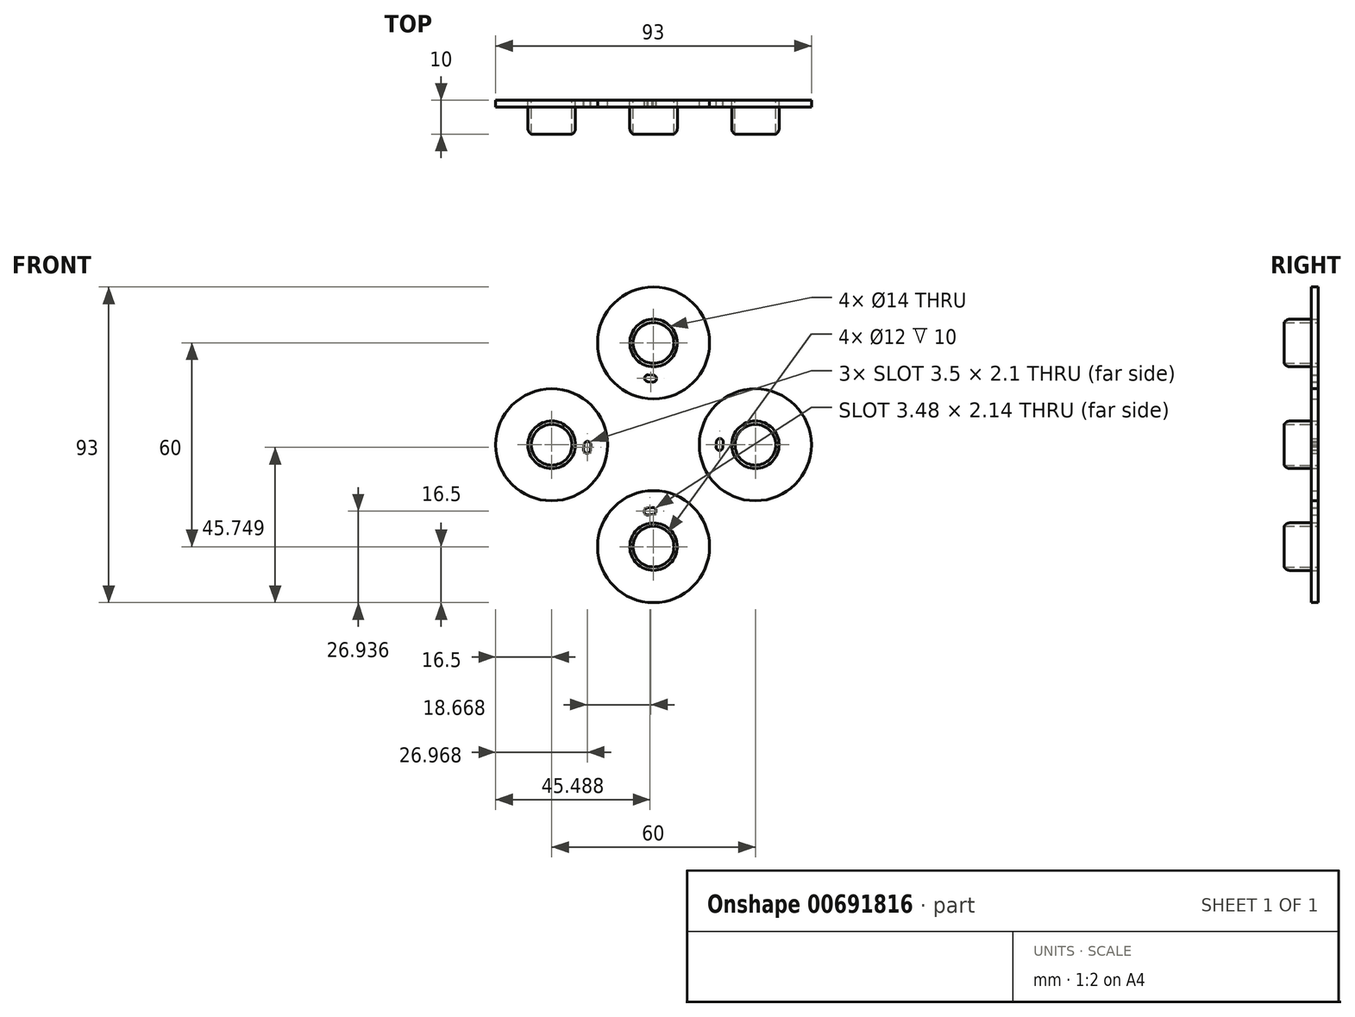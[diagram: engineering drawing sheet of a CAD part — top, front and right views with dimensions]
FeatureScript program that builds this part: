
annotation { "Feature Type Name" : "Feature", "Feature Type Description" : "" }
export const myFeature = defineFeature(function(context is Context, id is Id, definition is map)
    precondition{}
    {
        {
            var Q0;
            Q0=qCreatedBy(makeId("Front.planeOp"),FACE);
            var sketch = newSketch(context, id + "F0", { "sketchPlane" : qUnion([Q0])});
            skCircle(sketch, "E0", {"center": v(0, 0) * mm, "radius": 50 * mm});
            skCircle(sketch, "E1", {"center": v(0, 30) * mm, "radius": 16.5 * mm});
            skCircle(sketch, "E2", {"center": v(0, -30) * mm, "radius": 16.5 * mm});
            skCircle(sketch, "E3", {"center": v(-30, 0) * mm, "radius": 16.5 * mm});
            skCircle(sketch, "E4", {"center": v(30, 0) * mm, "radius": 16.5 * mm});
            skCircle(sketch, "E5", {"center": v(-30, 0) * mm, "radius": 12.5 * mm});
            skCircle(sketch, "E6", {"center": v(0, -30) * mm, "radius": 12.5 * mm});
            skCircle(sketch, "E7", {"center": v(30, 0) * mm, "radius": 12.5 * mm});
            skCircle(sketch, "E8", {"center": v(0, 30) * mm, "radius": 12.5 * mm});
            skCircle(sketch, "E9", {"center": v(-30, 0) * mm, "radius": 7 * mm});
            skCircle(sketch, "E10", {"center": v(0, 30) * mm, "radius": 7 * mm});
            skCircle(sketch, "E11", {"center": v(30, 0) * mm, "radius": 7 * mm});
            skCircle(sketch, "E12", {"center": v(0, -30) * mm, "radius": 7 * mm});
            skCircle(sketch, "E13", {"center": v(0, 30) * mm, "radius": 6 * mm});
            skCircle(sketch, "E14", {"center": v(-30, 0) * mm, "radius": 6 * mm});
            skCircle(sketch, "E15", {"center": v(0, -30) * mm, "radius": 6 * mm});
            skCircle(sketch, "E16", {"center": v(30, 0) * mm, "radius": 0.5 * mm});
            skCircle(sketch, "E17", {"center": v(-19.47, 0) * mm, "radius": 1 * mm});
            skCircle(sketch, "E18", {"center": v(-19.58, -1.5) * mm, "radius": 1 * mm});
            skLineSegment(sketch, "E19", {"start": v(-20.47, 0) * mm, "end": v(-20.58, -1.42) * mm});
            skLineSegment(sketch, "E20", {"start": v(-18.47, 0) * mm, "end": v(-18.6, -1.66) * mm});
            skCircle(sketch, "E21", {"center": v(-1.76, -19.65) * mm, "radius": 1 * mm});
            skCircle(sketch, "E22", {"center": v(-0.26, -19.48) * mm, "radius": 1 * mm});
            skLineSegment(sketch, "E23", {"start": v(-1.58, -20.63) * mm, "end": v(-0.15, -20.47) * mm});
            skLineSegment(sketch, "E24", {"start": v(-1.94, -18.67) * mm, "end": v(-0.3, -18.48) * mm});
            skLineSegment(sketch, "E25.0", {"start": v(-0.26, -19.48) * mm, "end": v(-0.28, -19.37) * mm, "construction": true});
            skCircle(sketch, "E26", {"center": v(19.54, 0.84) * mm, "radius": 1 * mm});
            skCircle(sketch, "E27", {"center": v(19.42, -0.66) * mm, "radius": 1 * mm});
            skLineSegment(sketch, "E28", {"start": v(18.54, 0.84) * mm, "end": v(18.43, -0.58) * mm});
            skLineSegment(sketch, "E29", {"start": v(20.54, 0.84) * mm, "end": v(20.41, -0.82) * mm});
            skCircle(sketch, "E30", {"center": v(-0.11, 19.5) * mm, "radius": 1 * mm});
            skCircle(sketch, "E31", {"center": v(-1.61, 19.61) * mm, "radius": 1 * mm});
            skLineSegment(sketch, "E32", {"start": v(-0.11, 20.5) * mm, "end": v(-1.54, 20.61) * mm});
            skLineSegment(sketch, "E33", {"start": v(-0.11, 18.5) * mm, "end": v(-1.78, 18.63) * mm});
            skCircle(sketch, "E34", {"center": v(30, 0) * mm, "radius": 6 * mm});
            skSolve(sketch);
        }
        {
            var Q0;
            Q0=makeQuery(id+"F0.imprint","IMPRINT",FACE,{"disambiguationData":[TD([[makeQuery(id+"F0.imprint","IMPRINT",EDGE,{"derivedFrom":sQuery(id+"F0.wireOp",EDGE,"E9")}),1.0]])]});
            var Q1;
            Q1=makeQuery(id+"F0.imprint","IMPRINT",FACE,{"disambiguationData":[TD([[makeQuery(id+"F0.imprint","IMPRINT",EDGE,{"derivedFrom":sQuery(id+"F0.wireOp",EDGE,"E10")}),1.0]])]});
            var Q2;
            Q2=makeQuery(id+"F0.imprint","IMPRINT",FACE,{"disambiguationData":[TD([[makeQuery(id+"F0.imprint","IMPRINT",EDGE,{"derivedFrom":sQuery(id+"F0.wireOp",EDGE,"E11")}),1.0]])]});
            var Q3;
            Q3=makeQuery(id+"F0.imprint","IMPRINT",FACE,{"disambiguationData":[TD([[makeQuery(id+"F0.imprint","IMPRINT",EDGE,{"derivedFrom":sQuery(id+"F0.wireOp",EDGE,"E12")}),1.0]])]});
            extrude(context, id + "F1", {"entities" : qUnion([Q0, Q1, Q2, Q3]), "depth" : 10 * mm, "offsetDistance" : 25 * mm});
        }
        {
            var Q0;
            Q0=makeQuery(id+"F0.imprint","IMPRINT",FACE,{"disambiguationData":[TD([[makeQuery(id+"F0.imprint","IMPRINT",EDGE,{"derivedFrom":sQuery(id+"F0.wireOp",EDGE,"E5")}),1.0]])]});
            var Q1;
            Q1=makeQuery(id+"F0.imprint","IMPRINT",FACE,{"disambiguationData":[TD([[makeQuery(id+"F0.imprint","IMPRINT",EDGE,{"derivedFrom":sQuery(id+"F0.wireOp",EDGE,"E8")}),1.0]])]});
            var Q2;
            Q2=makeQuery(id+"F0.imprint","IMPRINT",FACE,{"disambiguationData":[TD([[makeQuery(id+"F0.imprint","IMPRINT",EDGE,{"derivedFrom":sQuery(id+"F0.wireOp",EDGE,"E7")}),1.0]])]});
            var Q3;
            Q3=makeQuery(id+"F0.imprint","IMPRINT",FACE,{"disambiguationData":[TD([[makeQuery(id+"F0.imprint","IMPRINT",EDGE,{"derivedFrom":sQuery(id+"F0.wireOp",EDGE,"E6")}),1.0]])]});
            var Q4;
            Q4=makeQuery(id+"F0.imprint","IMPRINT",FACE,{"disambiguationData":[TD([[makeQuery(id+"F0.imprint","IMPRINT",EDGE,{"derivedFrom":sQuery(id+"F0.wireOp",EDGE,"E2")}),1.0]])]});
            var Q5;
            Q5=makeQuery(id+"F0.imprint","IMPRINT",FACE,{"disambiguationData":[TD([[makeQuery(id+"F0.imprint","IMPRINT",EDGE,{"derivedFrom":sQuery(id+"F0.wireOp",EDGE,"E4")}),1.0]])]});
            var Q6;
            Q6=makeQuery(id+"F0.imprint","IMPRINT",FACE,{"disambiguationData":[TD([[makeQuery(id+"F0.imprint","IMPRINT",EDGE,{"derivedFrom":sQuery(id+"F0.wireOp",EDGE,"E1")}),1.0]])]});
            var Q7;
            Q7=makeQuery(id+"F0.imprint","IMPRINT",FACE,{"disambiguationData":[TD([[makeQuery(id+"F0.imprint","IMPRINT",EDGE,{"derivedFrom":sQuery(id+"F0.wireOp",EDGE,"E3")}),1.0]])]});
            extrude(context, id + "F2", {"entities" : qUnion([Q0, Q1, Q2, Q3, Q4, Q5, Q6, Q7]), "depth" : 2 * mm, "offsetDistance" : 25 * mm});
        }
        {
            var Q0;
            Q0=makeQuery(id+"F1.opExtrude","CAP_EDGE",EDGE,{"disambiguationData":[OSD([sQuery(id+"F0.wireOp",EDGE,"E9")])],"isStart":false});
            var Q1;
            Q1=makeQuery(id+"F1.opExtrude","CAP_EDGE",EDGE,{"disambiguationData":[OSD([sQuery(id+"F0.wireOp",EDGE,"E10")])],"isStart":false});
            var Q2;
            Q2=makeQuery(id+"F1.opExtrude","CAP_EDGE",EDGE,{"disambiguationData":[OSD([sQuery(id+"F0.wireOp",EDGE,"E11")])],"isStart":false});
            var Q3;
            Q3=makeQuery(id+"F1.opExtrude","CAP_EDGE",EDGE,{"disambiguationData":[OSD([sQuery(id+"F0.wireOp",EDGE,"E12")])],"isStart":false});
            fillet(context, id + "F3", {"entities" : qUnion([Q0, Q1, Q2, Q3]), "radius" : 2 * mm, "tangentPropagation" : true, "allowEdgeOverflow" : false});
        }
    });
